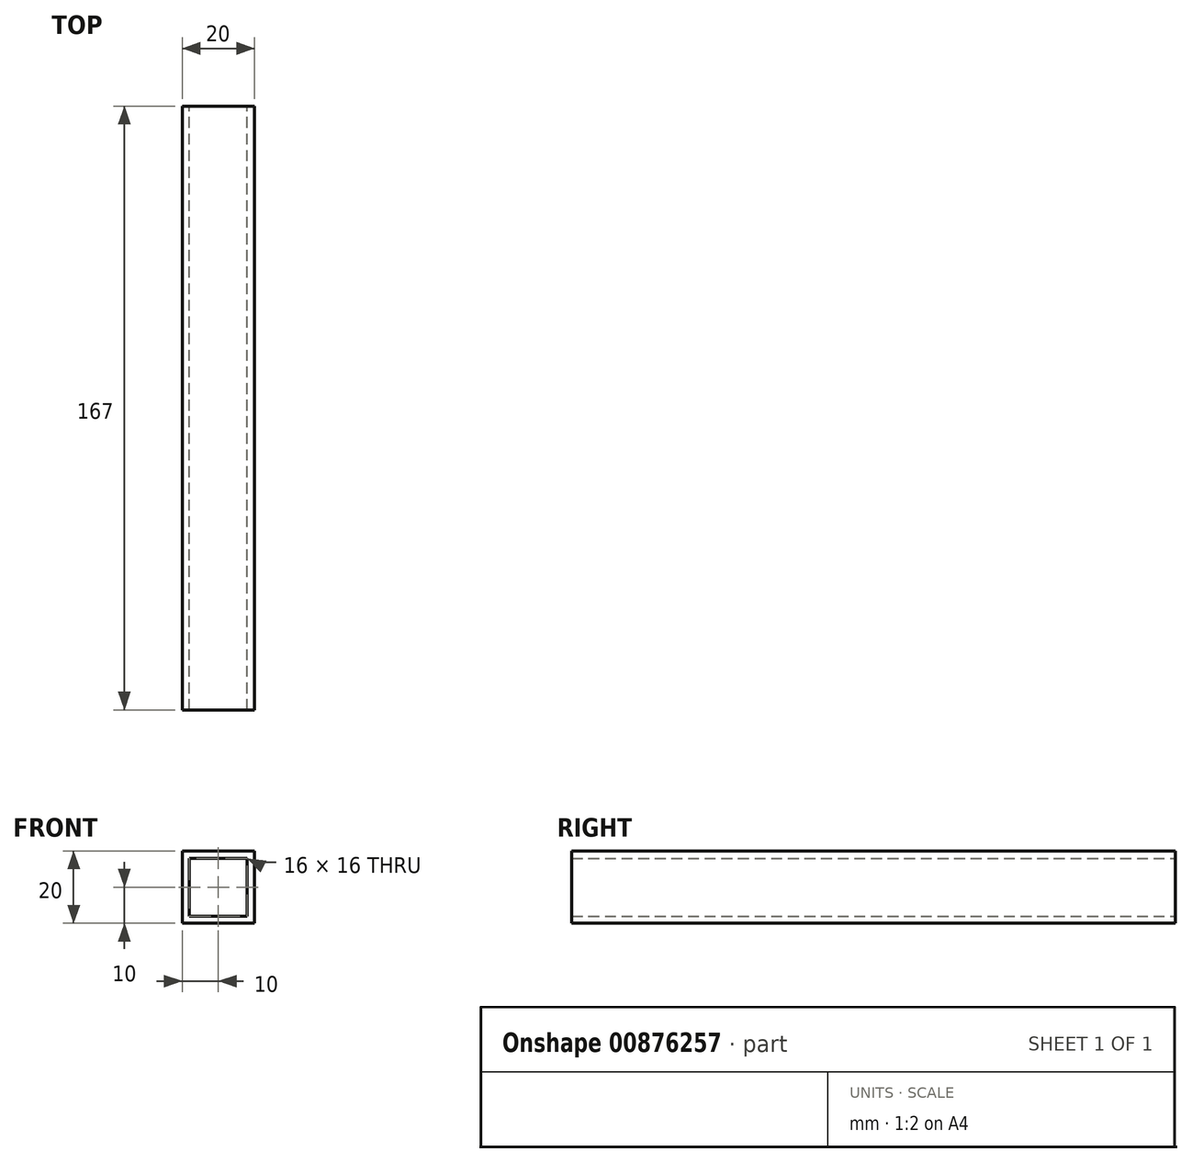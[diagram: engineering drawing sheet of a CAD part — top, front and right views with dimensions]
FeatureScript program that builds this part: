
annotation { "Feature Type Name" : "Feature", "Feature Type Description" : "" }
export const myFeature = defineFeature(function(context is Context, id is Id, definition is map)
    precondition{}
    {
        {
            var Q0;
            Q0=qCreatedBy(makeId("Front.planeOp"),FACE);
            var sketch = newSketch(context, id + "F0", { "sketchPlane" : qUnion([Q0])});
            skLineSegment(sketch, "E0.bottom", {"start": v(0, 0) * mm, "end": v(20, 0) * mm});
            skLineSegment(sketch, "E0.top", {"start": v(0, -20) * mm, "end": v(20, -20) * mm});
            skLineSegment(sketch, "E0.left", {"start": v(0, 0) * mm, "end": v(0, -20) * mm});
            skLineSegment(sketch, "E0.right", {"start": v(20, 0) * mm, "end": v(20, -20) * mm});
            skLineSegment(sketch, "E1.0", {"start": v(2, -2) * mm, "end": v(18, -2) * mm});
            skLineSegment(sketch, "E1.1", {"start": v(2, -2) * mm, "end": v(2, -18) * mm});
            skLineSegment(sketch, "E1.2", {"start": v(2, -18) * mm, "end": v(18, -18) * mm});
            skLineSegment(sketch, "E1.3", {"start": v(18, -2) * mm, "end": v(18, -18) * mm});
            skSolve(sketch);
        }
        {
            var Q0;
            Q0=makeQuery(id+"F0.imprint","IMPRINT",FACE,{"disambiguationData":[TD([[makeQuery(id+"F0.imprint","IMPRINT",EDGE,{"derivedFrom":sQuery(id+"F0.wireOp",EDGE,"E0.bottom")}),-1.0]])]});
            extrude(context, id + "F1", {"entities" : qUnion([Q0]), "depth" : 167 * mm, "offsetDistance" : 25.4 * mm});
        }
    });
